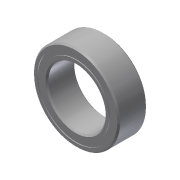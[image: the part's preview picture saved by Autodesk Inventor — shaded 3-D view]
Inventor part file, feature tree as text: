
AUTODESK INVENTOR PART (.ipt)
format: ipt  version: 2013 (Build 170138000, 138)  size: 547,328 bytes
history: native  units: in
note: dims shown in document units (in); Inventor stores cm internally (conversion verified against a paired STEP export)
features: imported_body x16, other x11, revolve x5
ambient origin geometry x8: Origin, YZ Plane, XZ Plane, XY Plane, X Axis, Y Axis, Z Axis, Center Point
feature tree (32):
  revolve  "Revolve1"  [1 undecoded]
  revolve  "Revolve3"  [1 undecoded]
  revolve  "Revolve4"  [1 undecoded]
  other  "CirPattern1[1]"
  other  "CirPattern1[2]"
  other  "CirPattern1[3]"
  other  "CirPattern1[4]"
  other  "CirPattern1[5]"
  other  "CirPattern1[6]"
  other  "CirPattern1[7]"
  other  "CirPattern1[8]"
  other  "CirPattern1[9]"
  other  "CirPattern1[10]"
  other  "CirPattern1[11]"
  revolve  "Revolve5[1]"  [1 undecoded]
  revolve  "Revolve5[2]"  [1 undecoded]
  imported_body  "Base1"
  imported_body  "Base2"
  imported_body  "Base3"
  imported_body  "Base4"
  imported_body  "Base5"
  imported_body  "Base6"
  imported_body  "Base7"
  imported_body  "Base8"
  imported_body  "Base9"
  imported_body  "Base10"
  imported_body  "Base11"
  imported_body  "Base12"
  imported_body  "Base13"
  imported_body  "Base14"
  imported_body  "Base15"
  imported_body  "Base16"
note: 5 required parameter values undecoded (feature->parameter linkage not recoverable at this tier; creation-order binding heuristic only, values carry confidence <= 0.55)
